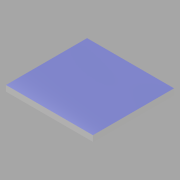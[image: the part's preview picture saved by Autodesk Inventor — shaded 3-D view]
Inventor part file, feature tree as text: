
AUTODESK INVENTOR PART (.ipt)
format: ipt  version: 2019 (Build 230136000, 136)  size: 98,304 bytes
history: native  units: mm
features: other x3, plane x1, extrude x1, sketch x1, projected_geometry x1
ambient origin geometry x8: Origin, YZ Plane, XZ Plane, XY Plane, X Axis, Y Axis, Z Axis, Center Point
bodies: Solid2 (feature_tree), Solid1 (feature_tree)
feature tree (7):
  other  "Absorption Filter 02.ipt"
  plane  "Work Plane1"
  extrude  "Extrusion1"  Depth=0.01mm
  other  "Solid2::Absorption Filter 02.ipt"
  other  "TaggingFeature1"
  sketch  "Sketch1"  dims[d0=10.0mm d1=0.01mm d2=0.5mm d3=0.0mm]
  projected_geometry  "Projected Loop1"
